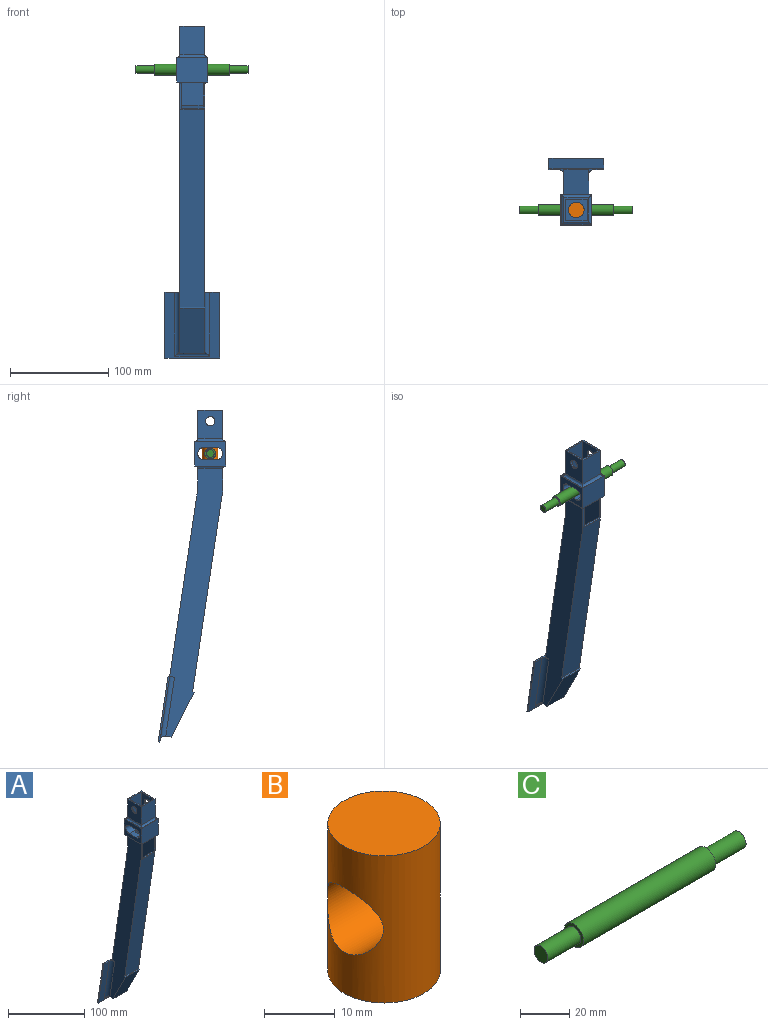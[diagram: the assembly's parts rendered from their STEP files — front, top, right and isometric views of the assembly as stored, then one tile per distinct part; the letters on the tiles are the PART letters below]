
ASSEMBLY  parts=3 mates=3
PART A: 70 faces, bbox 55.8x68.9x338.7 mm
  f0: plane 21.4x1.65mm, normal (0,-1,0), area 35.3mm2, adj f7,f8,f56,f68
  f1: plane 21.4x1.65mm, normal (0,-1,0), area 35.3mm2, adj f4,f5,f58,f67
  f2: plane 4.1x1.65mm, normal (0,0.15,-0.99), area 6.8mm2, adj f7,f8,f42,f63
  f3: plane 22.1x0.02mm, normal (0,0.15,-0.99), area 0.4mm2, adj f5,f6,f7,f36
  f4: plane 274.37x58.05mm, normal (1,0,0), area 6413.7mm2, adj f1,f9,f38,f39,f40,f42,f43,f44
  f5: plane 276.36x64.18mm, normal (-1,0,0), area 5903.1mm2, adj f1,f3,f6,f10,f36,f37,f40,f41
  f6: plane 23.85x22.1mm, normal (0,-1,0), area 527.1mm2, adj f3,f5,f7,f10
  f7: plane 276.36x64.18mm, normal (1,0,0), area 5903.1mm2, adj f0,f2,f3,f6,f10,f36,f37,f41
  f8: plane 274.37x58.05mm, normal (-1,0,0), area 6413.7mm2, adj f0,f2,f9,f38,f39,f42,f43,f44
  f9: plane 25.4x19.17mm, normal (0,1,0), area 486.9mm2, adj f4,f8,f59,f61
  f10: plane 31.75x31.75mm, normal (0,0,-1), area 462mm2, adj f5,f6,f7,f12,f13,f14,f15,f17
  f11: plane 31.75x31.75mm, normal (0,0,1), area 79mm2, adj f13,f14,f15,f17,f52,f53,f54,f55
  f12: cylinder r=7.94mm len=15.88mm, axis (0,0,-1), area 318.9mm2, adj f10,f19,f20,f21,f24
  f13: plane 31.75x25.4mm, normal (-1,0,0), area 518.5mm2, adj f10,f11,f14,f17,f19,f21,f22,f24
  f14: plane 31.75x25.4mm, normal (0,-1,0), area 806.5mm2, adj f10,f11,f13,f15
  f15: plane 31.75x25.4mm, normal (1,0,0), area 518.5mm2, adj f10,f11,f14,f17,f20,f21,f23,f24
  f16: cylinder r=7.94mm len=15.88mm, axis (0,0,-1), area 318.9mm2, adj f18,f21,f22,f23,f24
  f17: plane 31.75x25.4mm, normal (0,1,0), area 806.5mm2, adj f10,f11,f13,f15
  f18: plane 22.1x22.1mm, normal (0,0,1), area 290.4mm2, adj f16,f25,f26,f27,f32
  f19: plane 12.7x11.11mm, normal (0,0,1), area 112.9mm2, adj f12,f13,f21,f24
  f20: plane 12.7x11.11mm, normal (0,0,1), area 112.9mm2, adj f12,f15,f21,f24
  f21: cylinder r=6.35mm len=31.75mm, axis (1,0,0), area 612.6mm2, adj f12,f13,f15,f16,f19,f20,f22,f23
  f22: plane 12.7x11.11mm, normal (0,0,-1), area 112.9mm2, adj f13,f16,f21,f24
  f23: plane 12.7x11.11mm, normal (0,0,-1), area 112.9mm2, adj f15,f16,f21,f24
  f24: cylinder r=6.35mm len=31.75mm, axis (1,0,0), area 612.6mm2, adj f12,f13,f15,f16,f19,f20,f22,f23
  f25: plane 31.75x22.1mm, normal (0,-1,0), area 701.6mm2, adj f18,f26,f32,f33
  f26: plane 31.75x22.1mm, normal (-1,0,0), area 630.4mm2, adj f18,f25,f27,f33,f35
  f27: plane 31.75x22.1mm, normal (0,1,0), area 701.6mm2, adj f18,f26,f32,f33
  f28: plane 29.21x25.4mm, normal (-1,0,0), area 670.7mm2, adj f29,f31,f33,f34,f53
  f29: plane 29.21x25.4mm, normal (0,-1,0), area 741.9mm2, adj f28,f30,f33,f52
  f30: plane 29.21x25.4mm, normal (1,0,0), area 670.7mm2, adj f29,f31,f33,f35,f54
  f31: plane 29.21x25.4mm, normal (0,1,0), area 741.9mm2, adj f28,f30,f33,f55
  f32: plane 31.75x22.1mm, normal (1,0,0), area 630.4mm2, adj f18,f25,f27,f33,f34
  f33: plane 25.4x25.4mm, normal (0,0,1), area 156.8mm2, adj f25,f26,f27,f28,f29,f30,f31,f32
  f34: cylinder r=4.76mm len=9.53mm, axis (1,0,0), area 49.4mm2, adj f28,f32
  f35: cylinder r=4.76mm len=9.53mm, axis (1,0,0), area 49.4mm2, adj f26,f30
  f36: plane 252.51x37.88mm, normal (0,-0.99,-0.15), area 5642.3mm2, adj f3,f5,f7,f63
  f37: plane 207.47x31.12mm, normal (0,0.99,0.15), area 4636mm2, adj f5,f7,f41,f45
  f38: plane 202.2x30.33mm, normal (0,-0.99,-0.15), area 5193.3mm2, adj f4,f8,f43,f69
  f39: plane 189.27x28.39mm, normal (0,0.99,0.15), area 4861.2mm2, adj f4,f8,f46,f61
  f40: plane 4.1x1.65mm, normal (0,0.15,-0.99), area 6.8mm2, adj f4,f5,f42,f63
  f41: plane 22.1x1.63mm, normal (0,-0.15,0.99), area 36.4mm2, adj f5,f7,f37,f69
  f42: plane 25.4x1.47mm, normal (0,0.45,-0.89), area 41.9mm2, adj f2,f4,f8,f40,f44,f45
  f43: plane 25.4x1.47mm, normal (0,-0.45,0.89), area 41.9mm2, adj f4,f8,f38,f44
  f44: plane 46.29x25.4mm, normal (0,-0.89,-0.45), area 1316.2mm2, adj f4,f8,f42,f43
  f45: plane 41.56x22.1mm, normal (0,0.89,0.45), area 1028.2mm2, adj f5,f7,f37,f42
  f46: plane 55.81x6.66mm, normal (0,-0.15,0.99), area 103.2mm2, adj f4,f8,f39,f47,f49,f50,f51,f62
  f47: plane 67.07x11.66mm, normal (1,0,0), area 111.6mm2, adj f46,f48,f50,f51
  f48: plane 55.81x1.63mm, normal (0,0.15,-0.99), area 92.1mm2, adj f47,f49,f50,f51
  f49: plane 67.07x11.66mm, normal (-1,0,0), area 111.6mm2, adj f46,f48,f50,f51
  f50: plane 66.82x55.81mm, normal (0,0.99,0.15), area 3771.2mm2, adj f46,f47,f48,f49
  f51: plane 66.82x55.81mm, normal (0,-0.99,-0.15), area 1431.4mm2, adj f46,f47,f48,f49,f62,f63,f64
  f52: cylinder r=2.54mm len=30.48mm, axis (1,0,0), area 108.7mm2, adj f11,f29,f53,f54
  f53: cylinder r=2.54mm len=30.48mm, axis (0,-1,0), area 108.7mm2, adj f11,f28,f52,f55
  f54: cylinder r=2.54mm len=30.48mm, axis (0,1,0), area 108.7mm2, adj f11,f30,f52,f55
  f55: cylinder r=2.54mm len=30.48mm, axis (-1,0,0), area 108.7mm2, adj f11,f31,f53,f54
  f56: cylinder r=2.54mm len=4.19mm, axis (-1,0,0), area 10.3mm2, adj f0,f7,f10,f57
  f57: cylinder r=2.54mm len=30.48mm, axis (0,1,0), area 108.7mm2, adj f8,f10,f56,f59
  f58: cylinder r=2.54mm len=4.19mm, axis (-1,0,0), area 10.3mm2, adj f1,f5,f10,f60
  f59: cylinder r=2.54mm len=30.48mm, axis (1,0,0), area 108.7mm2, adj f9,f10,f57,f60
  f60: cylinder r=2.54mm len=30.48mm, axis (0,-1,0), area 108.7mm2, adj f4,f10,f58,f59
  f61: cylinder r=25.4mm len=25.4mm, axis (1,0,0), area 96.1mm2, adj f4,f8,f9,f39
  f62: cylinder r=5.08mm len=65.82mm, axis (0,-0.15,0.99), area 499.2mm2, adj f4,f46,f51,f63
  f63: cylinder r=5.08mm len=35.56mm, axis (-1,0,0), area 149mm2, adj f2,f5,f7,f36,f40,f51,f62,f64
  f64: cylinder r=5.08mm len=65.82mm, axis (0,-0.15,0.99), area 499.2mm2, adj f8,f46,f51,f63
  f65: plane 1.85x1.65mm, normal (0,-0.99,-0.1), area 3.1mm2, adj f7,f8,f68,f69
  f66: plane 1.85x1.65mm, normal (0,-0.99,-0.1), area 3.1mm2, adj f4,f5,f67,f69
  f67: cylinder r=12.7mm len=1.65mm, axis (-1,0,0), area 2.1mm2, adj f1,f4,f5,f66
  f68: cylinder r=12.7mm len=1.65mm, axis (-1,0,0), area 2.1mm2, adj f0,f7,f8,f65
  f69: cylinder r=12.7mm len=25.4mm, axis (-1,0,0), area 8.8mm2, adj f4,f5,f7,f8,f38,f41,f65,f66
PART B: 4 faces, bbox 15.9x15.9x25.4 mm
  f0: cylinder r=7.94mm len=25.4mm, axis (0,0,-1), area 1057.9mm2, adj f1,f2,f3
  f1: plane 15.88x15.88mm, normal (0,0,1), area 197.9mm2, adj f0
  f2: plane 15.88x15.88mm, normal (0,0,-1), area 197.9mm2, adj f0
  f3: cylinder r=5.56mm len=15.88mm, axis (-1,0,0), area 478.3mm2, adj f0
PART C: 7 faces, bbox 114.3x11.1x11.1 mm
  f0: cylinder r=5.56mm len=76.2mm, axis (-1,0,0), area 2660.2mm2, adj f1,f4
  f1: plane 11.11x11.11mm, normal (1,0,0), area 47.5mm2, adj f0,f2
  f2: cylinder r=3.97mm len=19.05mm, axis (-1,0,0), area 475mm2, adj f1,f3
  f3: plane 7.94x7.94mm, normal (1,0,0), area 49.5mm2, adj f2
  f4: plane 11.11x11.11mm, normal (-1,0,0), area 47.5mm2, adj f0,f5
  f5: cylinder r=3.97mm len=19.05mm, axis (1,0,0), area 475mm2, adj f4,f6
  f6: plane 7.94x7.94mm, normal (-1,0,0), area 49.5mm2, adj f5
PLACE A t=(-18.1,-1.17,23.44)mm
PLACE B t=(-18.1,-1.17,1.22)mm fixed
PLACE C rot(axis=(-1,0,0),101.3deg) t=(-18.41,-1.17,13.92)mm
MATE cylindrical A.f12 <-> B.f0  axis (0,0,-1) through (-18.1,-1.17,26.62)mm
MATE cylindrical C.f0 <-> B.f3  axis (-1,0,0) through (-18.41,-1.17,13.92)mm
MATE planar A.f11 <-> B.f0  axis (0,0,1) through (-33.98,-1.17,26.62)mm
